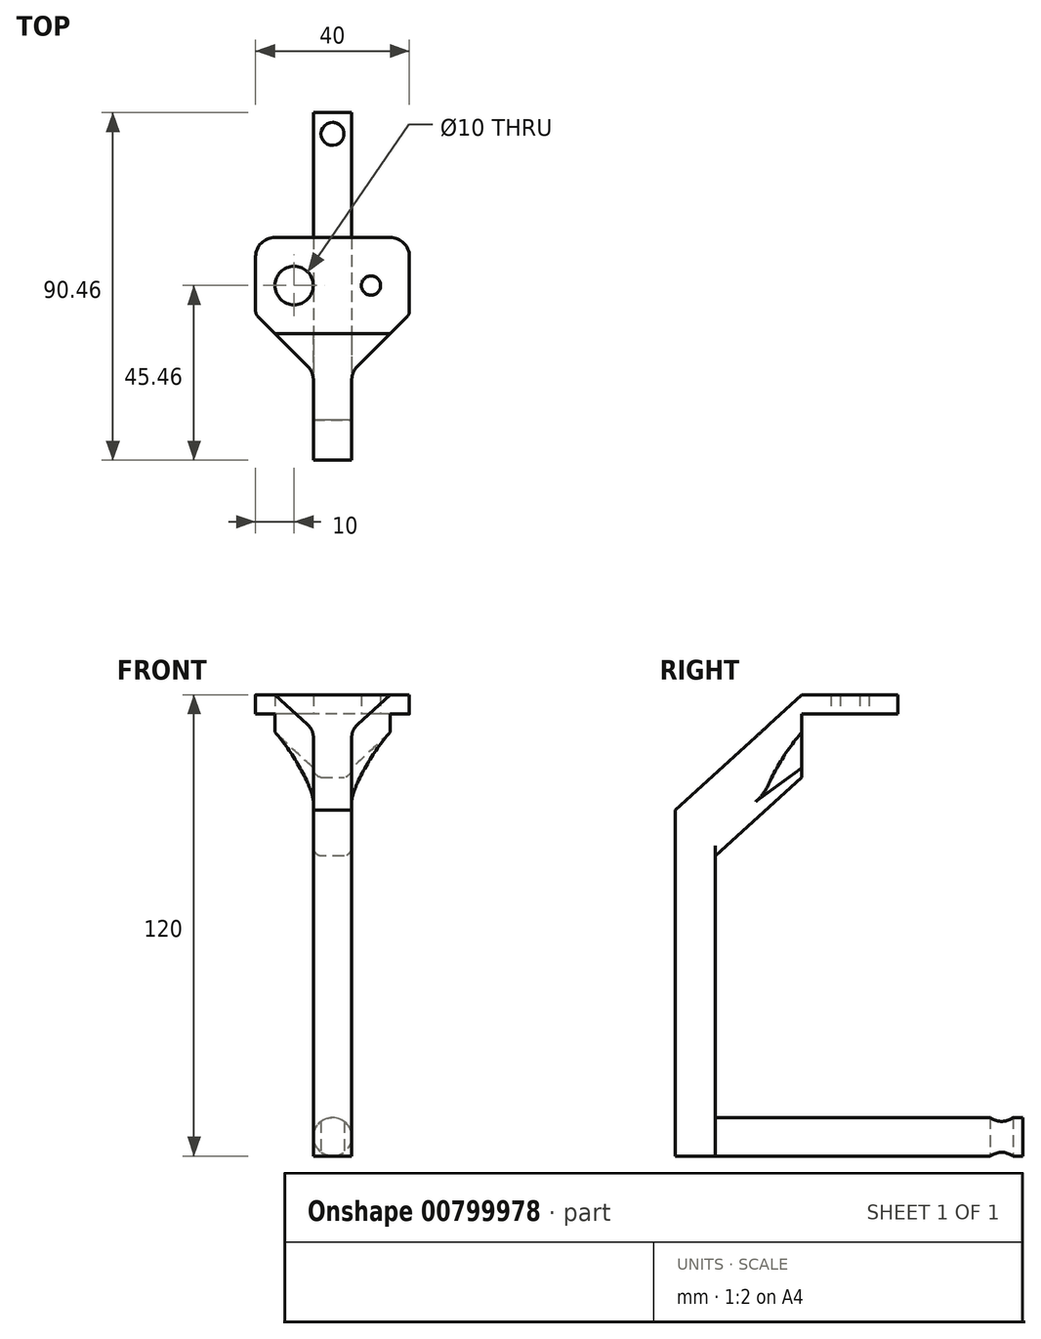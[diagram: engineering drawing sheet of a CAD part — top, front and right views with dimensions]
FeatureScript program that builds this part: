
annotation { "Feature Type Name" : "Feature", "Feature Type Description" : "" }
export const myFeature = defineFeature(function(context is Context, id is Id, definition is map)
    precondition{}
    {
        {
            var Q0;
            Q0=qCreatedBy(makeId("Top.planeOp"),FACE);
            var sketch = newSketch(context, id + "F0", { "sketchPlane" : qUnion([Q0])});
            skLineSegment(sketch, "E0.bottom", {"start": v(20, -12.5) * mm, "end": v(0, -12.5) * mm});
            skLineSegment(sketch, "E0.top", {"start": v(20, 12.5) * mm, "end": v(0, 12.5) * mm});
            skLineSegment(sketch, "E0.left", {"start": v(20, -12.5) * mm, "end": v(20, 12.5) * mm});
            skPoint(sketch, "E0.middle", {"position": v(0, 0) * mm});
            skCircle(sketch, "E1", {"center": v(10, 0) * mm, "radius": 5 * mm});
            skCircle(sketch, "E2", {"center": v(10, 0) * mm, "radius": 2.5 * mm});
            skPoint(sketch, "E3.orphan", {"position": v(-20, -12.5) * mm});
            skCircle(sketch, "E4.MirrorC", {"center": v(-10, 0) * mm, "radius": 5 * mm});
            skLineSegment(sketch, "E5.MirrorCS", {"start": v(-20, -12.5) * mm, "end": v(-20, 12.5) * mm});
            skCircle(sketch, "E6.MirrorC", {"center": v(-10, 0) * mm, "radius": 2.5 * mm});
            skLineSegment(sketch, "E7.MirrorCS", {"start": v(-20, -12.5) * mm, "end": v(0, -12.5) * mm});
            skLineSegment(sketch, "E8.MirrorCS", {"start": v(-20, 12.5) * mm, "end": v(0, 12.5) * mm});
            skSolve(sketch);
        }
        {
            var Q0;
            Q0=makeQuery(id+"F0.imprint","IMPRINT",FACE,{"disambiguationData":[TD([[makeQuery(id+"F0.imprint","IMPRINT",EDGE,{"derivedFrom":sQuery(id+"F0.wireOp",EDGE,"E0.bottom")}),-1.0]])]});
            var Q1;
            Q1=makeQuery(id+"F0.imprint","IMPRINT",FACE,{"disambiguationData":[TD([[makeQuery(id+"F0.imprint","IMPRINT",EDGE,{"derivedFrom":sQuery(id+"F0.wireOp",EDGE,"E4.MirrorC")}),-1.0]])]});
            var Q2;
            Q2=makeQuery(id+"F0.imprint","IMPRINT",FACE,{"disambiguationData":[TD([[makeQuery(id+"F0.imprint","IMPRINT",EDGE,{"derivedFrom":sQuery(id+"F0.wireOp",EDGE,"E1")}),1.0]])]});
            extrude(context, id + "F1", {"entities" : qUnion([Q0, Q1, Q2]), "depth" : 5 * mm, "offsetDistance" : 25 * mm});
        }
        {
            var Q0;
            Q0=qCreatedBy(makeId("Right.planeOp"),FACE);
            var sketch = newSketch(context, id + "F2", { "sketchPlane" : qUnion([Q0])});
            skLineSegment(sketch, "E9", {"start": v(-12.5, 5) * mm, "end": v(-45.46, -25) * mm});
            skLineSegment(sketch, "E10.0", {"start": v(5.57, 0) * mm, "end": v(-35, -36.93) * mm});
            skLineSegment(sketch, "E11", {"start": v(-35, -36.93) * mm, "end": v(-45.46, -25) * mm});
            skLineSegment(sketch, "E12", {"start": v(-12.5, 5) * mm, "end": v(5.57, 0) * mm});
            skLineSegment(sketch, "E13", {"start": v(-35, -36.93) * mm, "end": v(-35, -115) * mm});
            skLineSegment(sketch, "E14", {"start": v(-35, -115) * mm, "end": v(-45.46, -115) * mm});
            skLineSegment(sketch, "E15", {"start": v(-45.46, -115) * mm, "end": v(-45.46, -25) * mm});
            skSolve(sketch);
        }
        {
            var Q0;
            Q0=makeQuery(id+"F2.imprint","IMPRINT",FACE,{"disambiguationData":[TD([[makeQuery(id+"F2.imprint","IMPRINT",EDGE,{"derivedFrom":sQuery(id+"F2.wireOp",EDGE,"E9")}),1.0]])]});
            var Q1;
            Q1=makeQuery(id+"F2.imprint","IMPRINT",FACE,{"disambiguationData":[TD([[makeQuery(id+"F2.imprint","IMPRINT",EDGE,{"derivedFrom":sQuery(id+"F2.wireOp",EDGE,"E11")}),1.0]])]});
            extrude(context, id + "F3", {"entities" : qUnion([Q0, Q1]), "operationType" : NewBodyOperationType.ADD, "endBound" : BoundingType.SYMMETRIC, "depth" : 10 * mm, "offsetDistance" : 25 * mm});
        }
        {
            var Q0;
            Q0=makeQuery(id+"F3.opExtrude","CAP_EDGE",EDGE,{"disambiguationData":[OSD([sQuery(id+"F2.wireOp",EDGE,"E10.0")])],"isStart":true});
            var Q1;
            Q1=makeQuery(id+"F3.opExtrude","CAP_EDGE",EDGE,{"disambiguationData":[OSD([sQuery(id+"F2.wireOp",EDGE,"E10.0")])],"isStart":false});
            fillet(context, id + "F4", {"entities" : qUnion([Q0, Q1]), "radius" : 2 * mm, "tangentPropagation" : true, "allowEdgeOverflow" : false});
        }
        {
            var Q0;
            Q0=makeQuery(id+"F3.opExtrude","SWEPT_FACE",FACE,{"disambiguationData":[OSD([sQuery(id+"F2.wireOp",EDGE,"E13")])]});
            var sketch = newSketch(context, id + "F5", { "sketchPlane" : qUnion([Q0])});
            skCircle(sketch, "E16", {"center": v(0, -110) * mm, "radius": 5 * mm});
            skSolve(sketch);
        }
        {
            var Q0;
            {var subQ0=sQuery(id+"F5.wireOp",EDGE,"E16");var subQ1=sQuery(id+"F2.wireOp",EDGE,"E13");var subQ2=makeQuery(id+"F3.opExtrude","SWEPT_FACE",FACE,{"disambiguationData":[OSD([subQ1])]});var subQ3=makeQuery(id+"F4.opFillet","BLEND_EDGE",EDGE,{"blendedFrom":[makeQuery(id+"F3.opExtrude","CAP_EDGE",EDGE,{"disambiguationData":[OSD([subQ1])],"isStart":false}),subQ2],"blendedInto":[subQ2]});var subQ4=makeQuery(id+"F5.imprint","INTERSECT",VERTEX,{"disambiguationData":[OD(0.0)],"derivedFrom":[subQ3,subQ0]});Q0=makeQuery(id+"F5.imprint","IMPRINT",FACE,{"disambiguationData":[TD([[makeQuery(id+"F5.imprint","IMPRINT",EDGE,{"disambiguationData":[TD([[subQ4,1.0]])],"derivedFrom":subQ0}),1.0]])]});}
            var Q1;
            {var subQ0=sQuery(id+"F5.wireOp",EDGE,"E16");var subQ1=sQuery(id+"F2.wireOp",EDGE,"E13");var subQ2=makeQuery(id+"F4.opFillet","BLEND_EDGE",EDGE,{"blendedFrom":[makeQuery(id+"F3.opExtrude","CAP_EDGE",EDGE,{"disambiguationData":[OSD([subQ1])],"isStart":true}),makeQuery(id+"F3.opExtrude","SWEPT_FACE",FACE,{"disambiguationData":[OSD([subQ1])]})],"blendedInto":[makeQuery(id+"F3.opExtrude","SWEPT_FACE",FACE,{"disambiguationData":[OSD([subQ1])]})]});var subQ3=makeQuery(id+"F5.imprint","INTERSECT",VERTEX,{"disambiguationData":[OD(0.0)],"derivedFrom":[subQ2,subQ0]});Q1=makeQuery(id+"F5.imprint","IMPRINT",FACE,{"disambiguationData":[TD([[makeQuery(id+"F5.imprint","IMPRINT",EDGE,{"disambiguationData":[TD([[subQ3,1.0]])],"derivedFrom":subQ0}),1.0]])]});}
            var Q2;
            {var subQ0=sQuery(id+"F5.wireOp",EDGE,"E16");var subQ1=sQuery(id+"F2.wireOp",EDGE,"E13");var subQ2=makeQuery(id+"F4.opFillet","BLEND_EDGE",EDGE,{"blendedFrom":[makeQuery(id+"F3.opExtrude","CAP_EDGE",EDGE,{"disambiguationData":[OSD([subQ1])],"isStart":false}),makeQuery(id+"F3.opExtrude","SWEPT_FACE",FACE,{"disambiguationData":[OSD([subQ1])]})],"blendedInto":[makeQuery(id+"F3.opExtrude","SWEPT_FACE",FACE,{"disambiguationData":[OSD([subQ1])]})]});var subQ3=makeQuery(id+"F5.imprint","INTERSECT",VERTEX,{"disambiguationData":[OD(0.0)],"derivedFrom":[subQ2,subQ0]});Q2=makeQuery(id+"F5.imprint","IMPRINT",FACE,{"disambiguationData":[TD([[makeQuery(id+"F5.imprint","IMPRINT",EDGE,{"disambiguationData":[TD([[subQ3,-1.0]])],"derivedFrom":subQ0}),1.0]])]});}
            extrude(context, id + "F6", {"entities" : qUnion([Q0, Q1, Q2]), "operationType" : NewBodyOperationType.ADD, "depth" : 80 * mm, "offsetDistance" : 25 * mm});
        }
        {
            var Q0;
            Q0=makeQuery(id+"F3.boolean.opBoolean","INTERSECT",EDGE,{"derivedFrom":[makeQuery(id+"F1.opExtrude","CAP_FACE",FACE,{"disambiguationData":[OSD([sQuery(id+"F0.wireOp",EDGE,"E0.bottom"),sQuery(id+"F0.wireOp",EDGE,"E0.top"),sQuery(id+"F0.wireOp",EDGE,"E0.left"),sQuery(id+"F0.wireOp",EDGE,"E2"),sQuery(id+"F0.wireOp",EDGE,"E5.MirrorCS"),sQuery(id+"F0.wireOp",EDGE,"E6.MirrorC"),sQuery(id+"F0.wireOp",EDGE,"E7.MirrorCS"),sQuery(id+"F0.wireOp",EDGE,"E8.MirrorCS")])],"isStart":true}),makeQuery(id+"F3.opExtrude","CAP_FACE",FACE,{"disambiguationData":[OSD([sQuery(id+"F2.wireOp",EDGE,"E9"),sQuery(id+"F2.wireOp",EDGE,"E10.0"),sQuery(id+"F2.wireOp",EDGE,"E12"),sQuery(id+"F2.wireOp",EDGE,"E13"),sQuery(id+"F2.wireOp",EDGE,"E14"),sQuery(id+"F2.wireOp",EDGE,"E15")])],"isStart":false})]});
            chamfer(context, id + "F7", {"entities" : qUnion([Q0]), "width" : 15 * mm, "tangentPropagation" : true});
        }
        {
            var Q0;
            Q0=makeQuery(id+"F3.boolean.opBoolean","INTERSECT",EDGE,{"derivedFrom":[makeQuery(id+"F1.opExtrude","SWEPT_FACE",FACE,{"disambiguationData":[OSD([sQuery(id+"F0.wireOp",EDGE,"E0.bottom"),sQuery(id+"F0.wireOp",EDGE,"E7.MirrorCS")])]}),makeQuery(id+"F3.opExtrude","CAP_FACE",FACE,{"disambiguationData":[OSD([sQuery(id+"F2.wireOp",EDGE,"E9"),sQuery(id+"F2.wireOp",EDGE,"E10.0"),sQuery(id+"F2.wireOp",EDGE,"E12"),sQuery(id+"F2.wireOp",EDGE,"E13"),sQuery(id+"F2.wireOp",EDGE,"E14"),sQuery(id+"F2.wireOp",EDGE,"E15")])],"isStart":true})]});
            var Q1;
            Q1=makeQuery(id+"F3.boolean.opBoolean","INTERSECT",EDGE,{"derivedFrom":[makeQuery(id+"F1.opExtrude","SWEPT_FACE",FACE,{"disambiguationData":[OSD([sQuery(id+"F0.wireOp",EDGE,"E0.bottom"),sQuery(id+"F0.wireOp",EDGE,"E7.MirrorCS")])]}),makeQuery(id+"F3.opExtrude","CAP_FACE",FACE,{"disambiguationData":[OSD([sQuery(id+"F2.wireOp",EDGE,"E9"),sQuery(id+"F2.wireOp",EDGE,"E10.0"),sQuery(id+"F2.wireOp",EDGE,"E12"),sQuery(id+"F2.wireOp",EDGE,"E13"),sQuery(id+"F2.wireOp",EDGE,"E14"),sQuery(id+"F2.wireOp",EDGE,"E15")])],"isStart":false})]});
            chamfer(context, id + "F8", {"entities" : qUnion([Q0, Q1]), "width" : 10 * mm, "tangentPropagation" : true});
        }
        {
            var Q0;
            Q0=makeQuery(id+"F1.opExtrude","SWEPT_EDGE",EDGE,{"disambiguationData":[OSD([sQuery(id+"F0.wireOp",EDGE,"E5.MirrorCS"),sQuery(id+"F0.wireOp",EDGE,"E8.MirrorCS")])]});
            var Q1;
            Q1=makeQuery(id+"F1.opExtrude","SWEPT_EDGE",EDGE,{"disambiguationData":[OSD([sQuery(id+"F0.wireOp",EDGE,"E0.top"),sQuery(id+"F0.wireOp",EDGE,"E0.left")])]});
            fillet(context, id + "F9", {"entities" : qUnion([Q0, Q1]), "radius" : 5 * mm, "tangentPropagation" : true, "allowEdgeOverflow" : false});
        }
        {
            var Q0;
            Q0=makeQuery(id+"F1.opExtrude","SWEPT_EDGE",EDGE,{"disambiguationData":[OSD([sQuery(id+"F0.wireOp",EDGE,"E5.MirrorCS"),sQuery(id+"F0.wireOp",EDGE,"E7.MirrorCS")])]});
            var Q1;
            Q1=makeQuery(id+"F1.opExtrude","SWEPT_EDGE",EDGE,{"disambiguationData":[OSD([sQuery(id+"F0.wireOp",EDGE,"E0.bottom"),sQuery(id+"F0.wireOp",EDGE,"E0.left")])]});
            chamfer(context, id + "F10", {"entities" : qUnion([Q0, Q1]), "width" : 5 * mm, "tangentPropagation" : true});
        }
        {
            var Q0;
            {var subQ0=makeQuery(id+"F3.opExtrude","CAP_FACE",FACE,{"disambiguationData":[OSD([sQuery(id+"F2.wireOp",EDGE,"E9"),sQuery(id+"F2.wireOp",EDGE,"E10.0"),sQuery(id+"F2.wireOp",EDGE,"E12"),sQuery(id+"F2.wireOp",EDGE,"E13"),sQuery(id+"F2.wireOp",EDGE,"E14"),sQuery(id+"F2.wireOp",EDGE,"E15")])],"isStart":false});Q0=makeQuery(id+"F8.opChamfer","BLEND_EDGE",EDGE,{"blendedFrom":[makeQuery(id+"F3.boolean.opBoolean","INTERSECT",EDGE,{"derivedFrom":[makeQuery(id+"F1.opExtrude","SWEPT_FACE",FACE,{"disambiguationData":[OSD([sQuery(id+"F0.wireOp",EDGE,"E0.bottom"),sQuery(id+"F0.wireOp",EDGE,"E7.MirrorCS")])]}),subQ0]}),subQ0],"blendedInto":[subQ0]});}
            var Q1;
            {var subQ0=makeQuery(id+"F3.opExtrude","CAP_FACE",FACE,{"disambiguationData":[OSD([sQuery(id+"F2.wireOp",EDGE,"E9"),sQuery(id+"F2.wireOp",EDGE,"E10.0"),sQuery(id+"F2.wireOp",EDGE,"E12"),sQuery(id+"F2.wireOp",EDGE,"E13"),sQuery(id+"F2.wireOp",EDGE,"E14"),sQuery(id+"F2.wireOp",EDGE,"E15")])],"isStart":true});Q1=makeQuery(id+"F8.opChamfer","BLEND_EDGE",EDGE,{"blendedFrom":[makeQuery(id+"F3.boolean.opBoolean","INTERSECT",EDGE,{"derivedFrom":[makeQuery(id+"F1.opExtrude","SWEPT_FACE",FACE,{"disambiguationData":[OSD([sQuery(id+"F0.wireOp",EDGE,"E0.bottom"),sQuery(id+"F0.wireOp",EDGE,"E7.MirrorCS")])]}),subQ0]}),subQ0],"blendedInto":[subQ0]});}
            fillet(context, id + "F11", {"entities" : qUnion([Q0, Q1]), "radius" : 5 * mm, "tangentPropagation" : true, "allowEdgeOverflow" : false});
        }
        {
            var Q0;
            {var subQ0=sQuery(id+"F0.wireOp",EDGE,"E0.left");Q0=makeQuery(id+"F10.opChamfer","BLEND_EDGE",EDGE,{"blendedFrom":[makeQuery(id+"F1.opExtrude","SWEPT_EDGE",EDGE,{"disambiguationData":[OSD([sQuery(id+"F0.wireOp",EDGE,"E0.bottom"),subQ0])]}),makeQuery(id+"F1.opExtrude","SWEPT_FACE",FACE,{"disambiguationData":[OSD([subQ0])]})],"blendedInto":[makeQuery(id+"F1.opExtrude","SWEPT_FACE",FACE,{"disambiguationData":[OSD([subQ0])]})]});}
            var Q1;
            {var subQ0=sQuery(id+"F0.wireOp",EDGE,"E5.MirrorCS");Q1=makeQuery(id+"F10.opChamfer","BLEND_EDGE",EDGE,{"blendedFrom":[makeQuery(id+"F1.opExtrude","SWEPT_EDGE",EDGE,{"disambiguationData":[OSD([subQ0,sQuery(id+"F0.wireOp",EDGE,"E7.MirrorCS")])]}),makeQuery(id+"F1.opExtrude","SWEPT_FACE",FACE,{"disambiguationData":[OSD([subQ0])]})],"blendedInto":[makeQuery(id+"F1.opExtrude","SWEPT_FACE",FACE,{"disambiguationData":[OSD([subQ0])]})]});}
            fillet(context, id + "F12", {"entities" : qUnion([Q0, Q1]), "radius" : 2 * mm, "tangentPropagation" : true, "allowEdgeOverflow" : false});
        }
        {
            var Q0;
            Q0=makeQuery(id+"F0.imprint","IMPRINT",FACE,{"disambiguationData":[TD([[makeQuery(id+"F0.imprint","IMPRINT",EDGE,{"derivedFrom":sQuery(id+"F0.wireOp",EDGE,"E4.MirrorC")}),-1.0]])]});
            var Q1;
            Q1=makeQuery(id+"F0.imprint","IMPRINT",FACE,{"disambiguationData":[TD([[makeQuery(id+"F0.imprint","IMPRINT",EDGE,{"derivedFrom":sQuery(id+"F0.wireOp",EDGE,"E1")}),1.0]])]});
            extrude(context, id + "F13", {"entities" : qUnion([Q0, Q1]), "operationType" : NewBodyOperationType.REMOVE, "oppositeDirection" : true, "depth" : 25 * mm, "offsetDistance" : 25 * mm});
        }
        {
            var Q0;
            Q0=makeQuery(id+"F3.opExtrude","SWEPT_FACE",FACE,{"disambiguationData":[OSD([sQuery(id+"F2.wireOp",EDGE,"E14")])]});
            var sketch = newSketch(context, id + "F14", { "sketchPlane" : qUnion([Q0])});
            skCircle(sketch, "E17", {"center": v(0, -39.44) * mm, "radius": 3 * mm});
            skSolve(sketch);
        }
        {
            var Q0;
            Q0=makeQuery(id+"F14.imprint","IMPRINT",FACE,{"disambiguationData":[TD([[makeQuery(id+"F14.imprint","IMPRINT",EDGE,{"derivedFrom":sQuery(id+"F14.wireOp",EDGE,"E17")}),1.0]])]});
            extrude(context, id + "F15", {"entities" : qUnion([Q0]), "operationType" : NewBodyOperationType.REMOVE, "oppositeDirection" : true, "depth" : 25 * mm, "offsetDistance" : 25 * mm});
        }
    });
